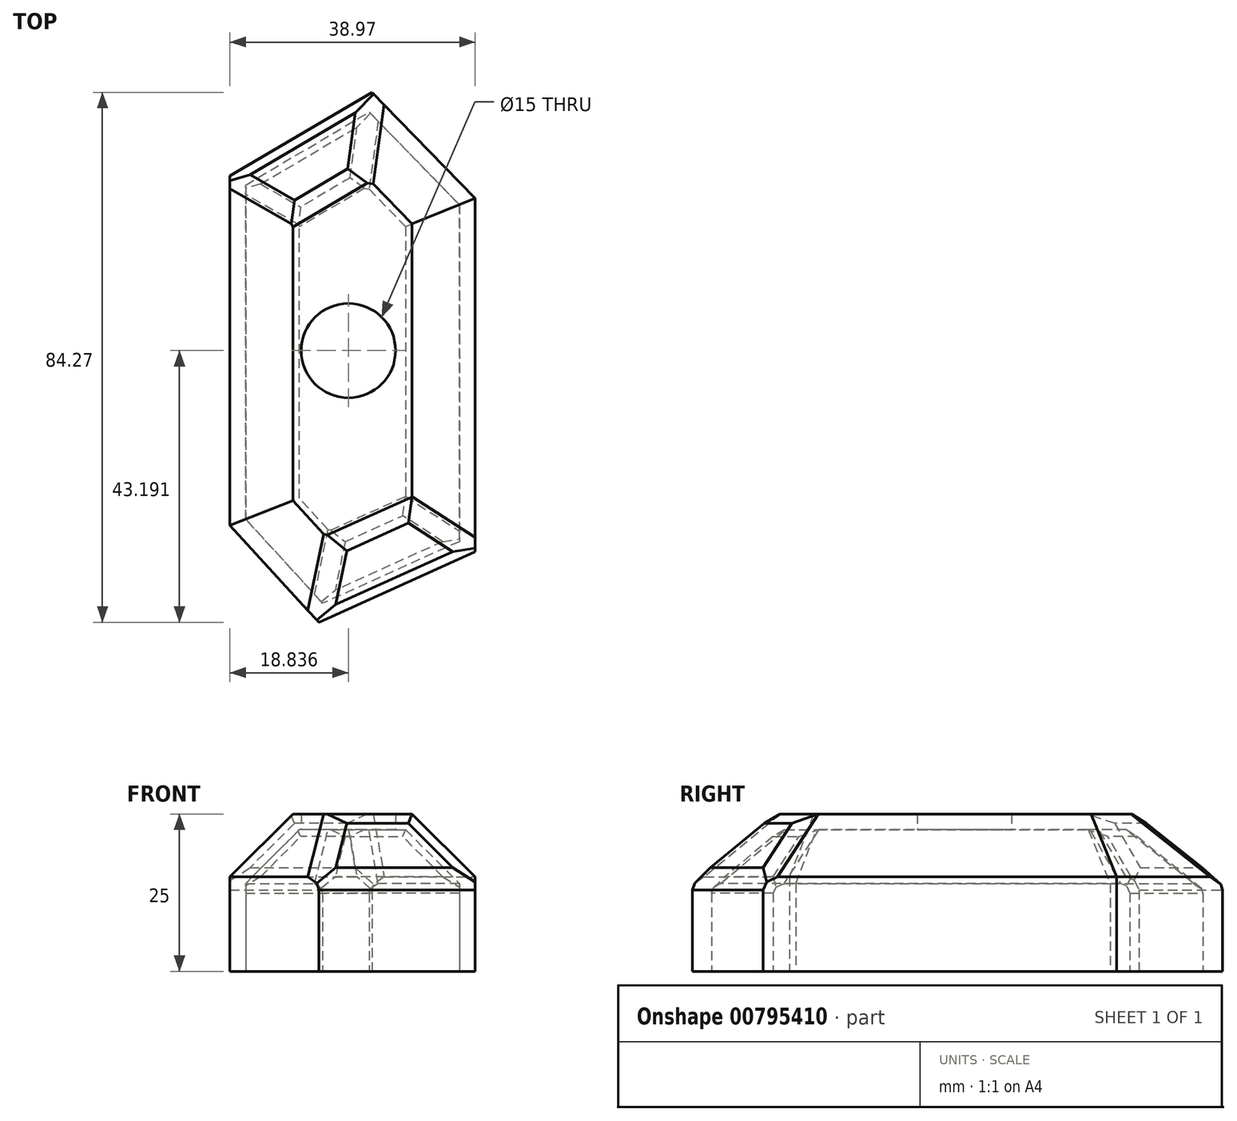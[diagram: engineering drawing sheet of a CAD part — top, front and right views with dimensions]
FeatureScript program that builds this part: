
annotation { "Feature Type Name" : "Feature", "Feature Type Description" : "" }
export const myFeature = defineFeature(function(context is Context, id is Id, definition is map)
    precondition{}
    {
        {
            var Q0;
            Q0=qCreatedBy(makeId("Top.planeOp"),FACE);
            var sketch = newSketch(context, id + "F0", { "sketchPlane" : qUnion([Q0])});
            skLineSegment(sketch, "E0", {"start": v(-38.97, 0) * mm, "end": v(-38.97, 34.67) * mm});
            skLineSegment(sketch, "E1", {"start": v(-38.97, 34.67) * mm, "end": v(-16.4, 47.98) * mm});
            skLineSegment(sketch, "E2", {"start": v(-16.4, 47.98) * mm, "end": v(0, 31.1) * mm});
            skLineSegment(sketch, "E3", {"start": v(0, 31.1) * mm, "end": v(0, -25.09) * mm});
            skLineSegment(sketch, "E4", {"start": v(0, -25.09) * mm, "end": v(-24.84, -36.29) * mm});
            skLineSegment(sketch, "E5", {"start": v(-24.84, -36.29) * mm, "end": v(-38.97, -20.86) * mm});
            skLineSegment(sketch, "E6", {"start": v(-38.97, -20.86) * mm, "end": v(-38.97, 0) * mm});
            skPoint(sketch, "E7", {"position": v(-20.13, 6.9) * mm});
            skSolve(sketch);
        }
        {
            var Q0;
            Q0=makeQuery(id+"F0.imprint","IMPRINT",FACE,{"disambiguationData":[TD([[makeQuery(id+"F0.imprint","IMPRINT",EDGE,{"derivedFrom":sQuery(id+"F0.wireOp",EDGE,"E0")}),-1.0]])]});
            extrude(context, id + "F1", {"entities" : qUnion([Q0]), "depth" : 25 * mm, "offsetDistance" : 25 * mm});
        }
        {
            var Q0;
            Q0=makeQuery(id+"F1.opExtrude","CAP_FACE",FACE,{"disambiguationData":[OSD([sQuery(id+"F0.wireOp",EDGE,"E0"),sQuery(id+"F0.wireOp",EDGE,"E1"),sQuery(id+"F0.wireOp",EDGE,"E2"),sQuery(id+"F0.wireOp",EDGE,"E3"),sQuery(id+"F0.wireOp",EDGE,"E4"),sQuery(id+"F0.wireOp",EDGE,"E5"),sQuery(id+"F0.wireOp",EDGE,"E6")])],"isStart":false});
            chamfer(context, id + "F2", {"entities" : qUnion([Q0]), "width" : 10 * mm, "tangentPropagation" : true});
        }
        {
            var Q0;
            Q0=makeQuery(id+"F2.opChamfer","BLEND_FACE",FACE,{"disambiguationData":[OSD([sQuery(id+"F0.wireOp",EDGE,"E1")])]});
            var Q1;
            Q1=makeQuery(id+"F2.opChamfer","BLEND_FACE",FACE,{"disambiguationData":[OSD([sQuery(id+"F0.wireOp",EDGE,"E4")])]});
            chamfer(context, id + "F3", {"entities" : qUnion([Q0, Q1]), "width" : 5 * mm, "tangentPropagation" : true});
        }
        {
            var Q0;
            Q0=makeQuery(id+"F1.opExtrude","CAP_FACE",FACE,{"disambiguationData":[OSD([sQuery(id+"F0.wireOp",EDGE,"E0"),sQuery(id+"F0.wireOp",EDGE,"E1"),sQuery(id+"F0.wireOp",EDGE,"E2"),sQuery(id+"F0.wireOp",EDGE,"E3"),sQuery(id+"F0.wireOp",EDGE,"E4"),sQuery(id+"F0.wireOp",EDGE,"E5"),sQuery(id+"F0.wireOp",EDGE,"E6")])],"isStart":true});
            shell(context, id + "F4", {"entities" : qUnion([Q0]), "thickness" : 2.5 * mm});
        }
        {
            var Q0;
            Q0=sQuery(id+"F0.wireOp",VERTEX,"E7");
            var Q1;
            Q1=makeQuery(id+"F1.opExtrude","SWEPT_BODY",BODY,{"disambiguationData":[OSD([sQuery(id+"F0.wireOp",EDGE,"E0"),sQuery(id+"F0.wireOp",EDGE,"E1"),sQuery(id+"F0.wireOp",EDGE,"E2"),sQuery(id+"F0.wireOp",EDGE,"E3"),sQuery(id+"F0.wireOp",EDGE,"E4"),sQuery(id+"F0.wireOp",EDGE,"E5"),sQuery(id+"F0.wireOp",EDGE,"E6")])]});
            hole(context, id + "F5", {"style" : HoleStyle.SIMPLE, "endStyle" : HoleEndStyle.THROUGH, "oppositeDirection" : true, "holeDiameter" : 15 * mm, "majorDiameter" : 5 * mm, "isTappedThrough" : true, "tappedDepth" : 12 * mm, "tapClearance" : 3, "locations" : qUnion([Q0]), "scope" : qUnion([Q1])});
        }
    });
